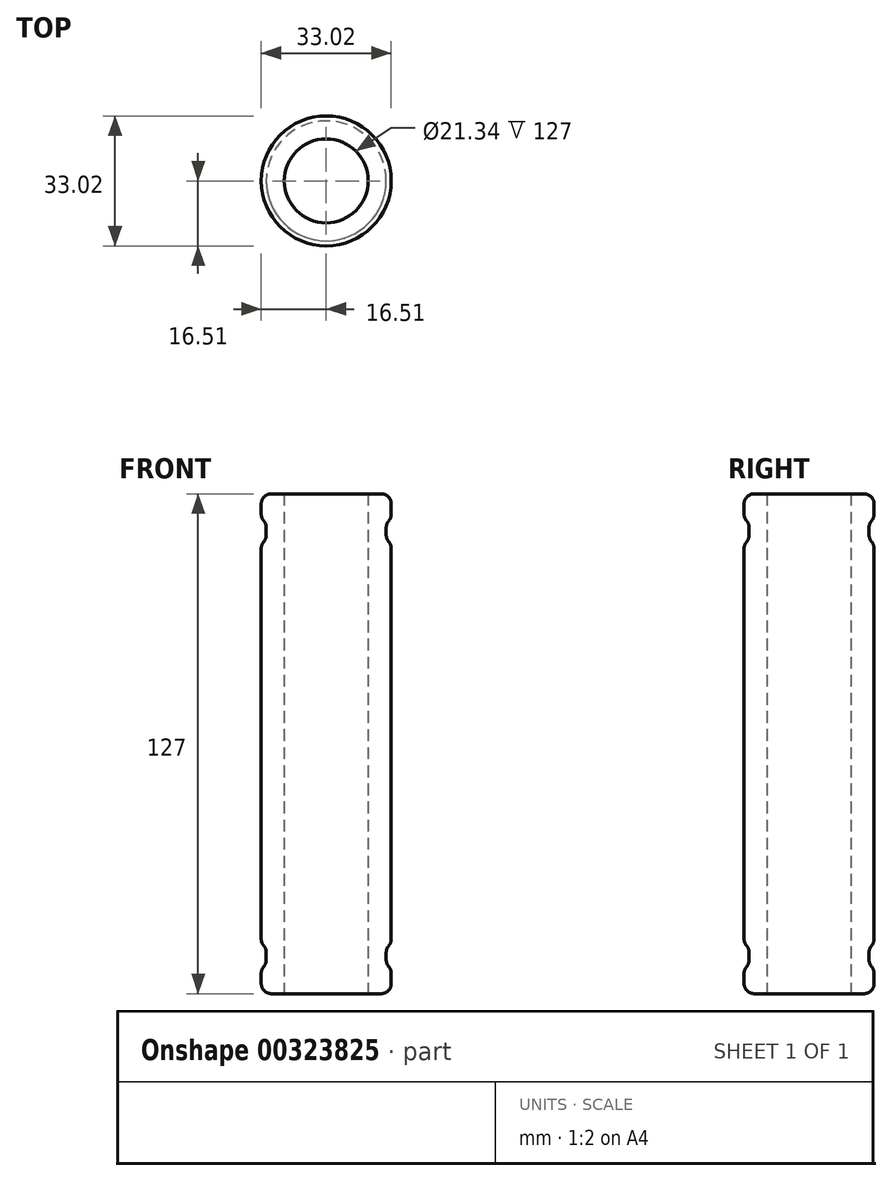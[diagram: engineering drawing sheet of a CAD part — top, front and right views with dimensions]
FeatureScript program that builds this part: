
annotation { "Feature Type Name" : "Feature", "Feature Type Description" : "" }
export const myFeature = defineFeature(function(context is Context, id is Id, definition is map)
    precondition{}
    {
        {
            var Q0;
            Q0=qCreatedBy(makeId("Top.planeOp"),FACE);
            var sketch = newSketch(context, id + "F0", { "sketchPlane" : qUnion([Q0])});
            skCircle(sketch, "E0", {"center": v(0, 0) * mm, "radius": 10.67 * mm});
            skCircle(sketch, "E1", {"center": v(0, 0) * mm, "radius": 16.51 * mm});
            skSolve(sketch);
        }
        {
            var Q0;
            Q0=makeQuery(id+"F0.imprint","IMPRINT",FACE,{"disambiguationData":[TD([[makeQuery(id+"F0.imprint","IMPRINT",EDGE,{"derivedFrom":sQuery(id+"F0.wireOp",EDGE,"E0")}),-1.0]])]});
            extrude(context, id + "F1", {"entities" : qUnion([Q0]), "depth" : 127 * mm});
        }
        {
            var Q0;
            Q0=makeQuery(id+"F1.opExtrude","CAP_FACE",FACE,{"disambiguationData":[OSD([sQuery(id+"F0.wireOp",EDGE,"E0"),sQuery(id+"F0.wireOp",EDGE,"E1")])],"isStart":false});
            cPlane(context, id + "F2", {"entities" : qUnion([Q0]), "cplaneType" : CPlaneType.OFFSET, "offset" : 12.7 * mm, "oppositeDirection" : true, "width" : 152.4 * mm, "height" : 152.4 * mm});
        }
        {
            var Q0;
            Q0=qCreatedBy(id+"F2.planeOp",FACE);
            var sketch = newSketch(context, id + "F3", { "sketchPlane" : qUnion([Q0])});
            skCircle(sketch, "E2", {"center": v(0, 0) * mm, "radius": 15.24 * mm});
            skCircle(sketch, "E3", {"center": v(0, 0) * mm, "radius": 16.96 * mm});
            skSolve(sketch);
        }
        {
            var Q0;
            Q0=qSketchRegion(id+"F3",true);
            extrude(context, id + "F4", {"entities" : qUnion([Q0]), "operationType" : NewBodyOperationType.REMOVE, "depth" : 6.35 * mm});
        }
        {
            var Q0;
            Q0=makeQuery(id+"F1.opExtrude","CAP_FACE",FACE,{"disambiguationData":[OSD([sQuery(id+"F0.wireOp",EDGE,"E0"),sQuery(id+"F0.wireOp",EDGE,"E1")])],"isStart":true});
            cPlane(context, id + "F5", {"entities" : qUnion([Q0]), "cplaneType" : CPlaneType.OFFSET, "offset" : 12.7 * mm, "oppositeDirection" : true, "width" : 152.4 * mm, "height" : 152.4 * mm});
        }
        {
            var Q0;
            Q0=qCreatedBy(id+"F5.planeOp",FACE);
            var sketch = newSketch(context, id + "F6", { "sketchPlane" : qUnion([Q0])});
            skCircle(sketch, "E4", {"center": v(0, 0) * mm, "radius": 15.24 * mm});
            skCircle(sketch, "E5", {"center": v(0, 0) * mm, "radius": 19.45 * mm});
            skSolve(sketch);
        }
        {
            var Q0;
            Q0=makeQuery(id+"F6.imprint","IMPRINT",FACE,{"disambiguationData":[TD([[makeQuery(id+"F6.imprint","IMPRINT",EDGE,{"derivedFrom":sQuery(id+"F6.wireOp",EDGE,"E4")}),-1.0]])]});
            extrude(context, id + "F7", {"entities" : qUnion([Q0]), "operationType" : NewBodyOperationType.REMOVE, "depth" : 6.35 * mm});
        }
        {
            var Q0;
            Q0=makeQuery(id+"F1.opExtrude","CAP_EDGE",EDGE,{"disambiguationData":[OSD([sQuery(id+"F0.wireOp",EDGE,"E1")])],"isStart":true});
            fillet(context, id + "F8", {"entities" : qUnion([Q0]), "radius" : 2.54 * mm, "tangentPropagation" : true, "allowEdgeOverflow" : false});
        }
        {
            var Q0;
            Q0=makeQuery(id+"F7.boolean.opBoolean","COPY",EDGE,{"derivedFrom":makeQuery(id+"F7.opExtrude","CAP_EDGE",EDGE,{"disambiguationData":[OSD([sQuery(id+"F6.wireOp",EDGE,"E4")])],"isStart":true})});
            fillet(context, id + "F9", {"entities" : qUnion([Q0]), "radius" : 2.54 * mm, "tangentPropagation" : true, "allowEdgeOverflow" : false});
        }
        {
            var Q0;
            Q0=makeQuery(id+"F7.boolean.opBoolean","COPY",EDGE,{"derivedFrom":makeQuery(id+"F7.opExtrude","CAP_EDGE",EDGE,{"disambiguationData":[OSD([sQuery(id+"F6.wireOp",EDGE,"E4")])],"isStart":false})});
            fillet(context, id + "F10", {"entities" : qUnion([Q0]), "radius" : 2.54 * mm, "tangentPropagation" : true, "allowEdgeOverflow" : false});
        }
        {
            var Q0;
            {var subQ0=makeQuery(id+"F4.opExtrude","CAP_FACE",FACE,{"disambiguationData":[OSD([sQuery(id+"F3.wireOp",EDGE,"E2"),sQuery(id+"F3.wireOp",EDGE,"E3")])],"isStart":true});var subQ1=sQuery(id+"F6.wireOp",EDGE,"E4");var subQ2=sQuery(id+"F0.wireOp",EDGE,"E1");Q0=makeQuery(id+"F9.opFillet","BLEND_EDGE",EDGE,{"blendedFrom":[makeQuery(id+"F7.boolean.opBoolean","COPY",EDGE,{"derivedFrom":makeQuery(id+"F7.opExtrude","CAP_EDGE",EDGE,{"disambiguationData":[OSD([subQ1])],"isStart":true})}),makeQuery(id+"F7.boolean.opBoolean","SPLIT",FACE,{"disambiguationData":[TD([makeQuery(id+"F4.boolean.opBoolean","COPY",FACE,{"derivedFrom":subQ0})])],"derivedFrom":makeQuery(id+"F4.boolean.opBoolean","SPLIT",FACE,{"disambiguationData":[TD([makeQuery(id+"F1.opExtrude","CAP_FACE",FACE,{"disambiguationData":[OSD([sQuery(id+"F0.wireOp",EDGE,"E0"),subQ2])],"isStart":true})])],"derivedFrom":makeQuery(id+"F1.opExtrude","SWEPT_FACE",FACE,{"disambiguationData":[OSD([subQ2])]})})})],"blendedInto":[makeQuery(id+"F7.boolean.opBoolean","SPLIT",FACE,{"disambiguationData":[TD([makeQuery(id+"F4.boolean.opBoolean","COPY",FACE,{"derivedFrom":subQ0})])],"derivedFrom":makeQuery(id+"F4.boolean.opBoolean","SPLIT",FACE,{"disambiguationData":[TD([makeQuery(id+"F1.opExtrude","CAP_FACE",FACE,{"disambiguationData":[OSD([sQuery(id+"F0.wireOp",EDGE,"E0"),subQ2])],"isStart":true})])],"derivedFrom":makeQuery(id+"F1.opExtrude","SWEPT_FACE",FACE,{"disambiguationData":[OSD([subQ2])]})})})]});}
            var Q1;
            {var subQ0=sQuery(id+"F0.wireOp",EDGE,"E1");var subQ1=makeQuery(id+"F1.opExtrude","CAP_FACE",FACE,{"disambiguationData":[OSD([sQuery(id+"F0.wireOp",EDGE,"E0"),subQ0])],"isStart":true});var subQ2=sQuery(id+"F6.wireOp",EDGE,"E4");Q1=makeQuery(id+"F10.opFillet","BLEND_EDGE",EDGE,{"blendedFrom":[makeQuery(id+"F7.boolean.opBoolean","COPY",EDGE,{"derivedFrom":makeQuery(id+"F7.opExtrude","CAP_EDGE",EDGE,{"disambiguationData":[OSD([subQ2])],"isStart":false})}),makeQuery(id+"F7.boolean.opBoolean","SPLIT",FACE,{"disambiguationData":[TD([subQ1])],"derivedFrom":makeQuery(id+"F4.boolean.opBoolean","SPLIT",FACE,{"disambiguationData":[TD([subQ1])],"derivedFrom":makeQuery(id+"F1.opExtrude","SWEPT_FACE",FACE,{"disambiguationData":[OSD([subQ0])]})})})],"blendedInto":[makeQuery(id+"F7.boolean.opBoolean","SPLIT",FACE,{"disambiguationData":[TD([subQ1])],"derivedFrom":makeQuery(id+"F4.boolean.opBoolean","SPLIT",FACE,{"disambiguationData":[TD([subQ1])],"derivedFrom":makeQuery(id+"F1.opExtrude","SWEPT_FACE",FACE,{"disambiguationData":[OSD([subQ0])]})})})]});}
            fillet(context, id + "F11", {"entities" : qUnion([Q0, Q1]), "radius" : 2.54 * mm, "tangentPropagation" : true, "allowEdgeOverflow" : false});
        }
        {
            var Q0;
            Q0=makeQuery(id+"F1.opExtrude","CAP_EDGE",EDGE,{"disambiguationData":[OSD([sQuery(id+"F0.wireOp",EDGE,"E1")])],"isStart":false});
            var Q1;
            Q1=makeQuery(id+"F4.boolean.opBoolean","COPY",EDGE,{"derivedFrom":makeQuery(id+"F4.opExtrude","CAP_EDGE",EDGE,{"disambiguationData":[OSD([sQuery(id+"F3.wireOp",EDGE,"E2")])],"isStart":true})});
            fillet(context, id + "F12", {"entities" : qUnion([Q0, Q1]), "radius" : 2.54 * mm, "tangentPropagation" : true, "allowEdgeOverflow" : false});
        }
        {
            var Q0;
            Q0=makeQuery(id+"F4.boolean.opBoolean","COPY",EDGE,{"derivedFrom":makeQuery(id+"F4.opExtrude","CAP_EDGE",EDGE,{"disambiguationData":[OSD([sQuery(id+"F3.wireOp",EDGE,"E2")])],"isStart":false})});
            fillet(context, id + "F13", {"entities" : qUnion([Q0]), "radius" : 2.54 * mm, "tangentPropagation" : true, "allowEdgeOverflow" : false});
        }
        {
            var Q0;
            {var subQ0=sQuery(id+"F0.wireOp",EDGE,"E1");var subQ1=sQuery(id+"F3.wireOp",EDGE,"E2");Q0=makeQuery(id+"F13.opFillet","BLEND_EDGE",EDGE,{"blendedFrom":[makeQuery(id+"F4.boolean.opBoolean","COPY",EDGE,{"derivedFrom":makeQuery(id+"F4.opExtrude","CAP_EDGE",EDGE,{"disambiguationData":[OSD([subQ1])],"isStart":false})}),makeQuery(id+"F4.boolean.opBoolean","SPLIT",FACE,{"disambiguationData":[TD([makeQuery(id+"F1.opExtrude","CAP_FACE",FACE,{"disambiguationData":[OSD([sQuery(id+"F0.wireOp",EDGE,"E0"),subQ0])],"isStart":false})])],"derivedFrom":makeQuery(id+"F1.opExtrude","SWEPT_FACE",FACE,{"disambiguationData":[OSD([subQ0])]})})],"blendedInto":[makeQuery(id+"F4.boolean.opBoolean","SPLIT",FACE,{"disambiguationData":[TD([makeQuery(id+"F1.opExtrude","CAP_FACE",FACE,{"disambiguationData":[OSD([sQuery(id+"F0.wireOp",EDGE,"E0"),subQ0])],"isStart":false})])],"derivedFrom":makeQuery(id+"F1.opExtrude","SWEPT_FACE",FACE,{"disambiguationData":[OSD([subQ0])]})})]});}
            var Q1;
            {var subQ0=sQuery(id+"F3.wireOp",EDGE,"E2");var subQ1=makeQuery(id+"F4.opExtrude","CAP_FACE",FACE,{"disambiguationData":[OSD([subQ0,sQuery(id+"F3.wireOp",EDGE,"E3")])],"isStart":true});var subQ2=sQuery(id+"F0.wireOp",EDGE,"E1");Q1=makeQuery(id+"F12.opFillet","BLEND_EDGE",EDGE,{"blendedFrom":[makeQuery(id+"F4.boolean.opBoolean","COPY",EDGE,{"derivedFrom":makeQuery(id+"F4.opExtrude","CAP_EDGE",EDGE,{"disambiguationData":[OSD([subQ0])],"isStart":true})}),makeQuery(id+"F7.boolean.opBoolean","SPLIT",FACE,{"disambiguationData":[TD([makeQuery(id+"F4.boolean.opBoolean","COPY",FACE,{"derivedFrom":subQ1})])],"derivedFrom":makeQuery(id+"F4.boolean.opBoolean","SPLIT",FACE,{"disambiguationData":[TD([makeQuery(id+"F1.opExtrude","CAP_FACE",FACE,{"disambiguationData":[OSD([sQuery(id+"F0.wireOp",EDGE,"E0"),subQ2])],"isStart":true})])],"derivedFrom":makeQuery(id+"F1.opExtrude","SWEPT_FACE",FACE,{"disambiguationData":[OSD([subQ2])]})})})],"blendedInto":[makeQuery(id+"F7.boolean.opBoolean","SPLIT",FACE,{"disambiguationData":[TD([makeQuery(id+"F4.boolean.opBoolean","COPY",FACE,{"derivedFrom":subQ1})])],"derivedFrom":makeQuery(id+"F4.boolean.opBoolean","SPLIT",FACE,{"disambiguationData":[TD([makeQuery(id+"F1.opExtrude","CAP_FACE",FACE,{"disambiguationData":[OSD([sQuery(id+"F0.wireOp",EDGE,"E0"),subQ2])],"isStart":true})])],"derivedFrom":makeQuery(id+"F1.opExtrude","SWEPT_FACE",FACE,{"disambiguationData":[OSD([subQ2])]})})})]});}
            fillet(context, id + "F14", {"entities" : qUnion([Q0, Q1]), "radius" : 2.54 * mm, "tangentPropagation" : true, "allowEdgeOverflow" : false});
        }
    });
